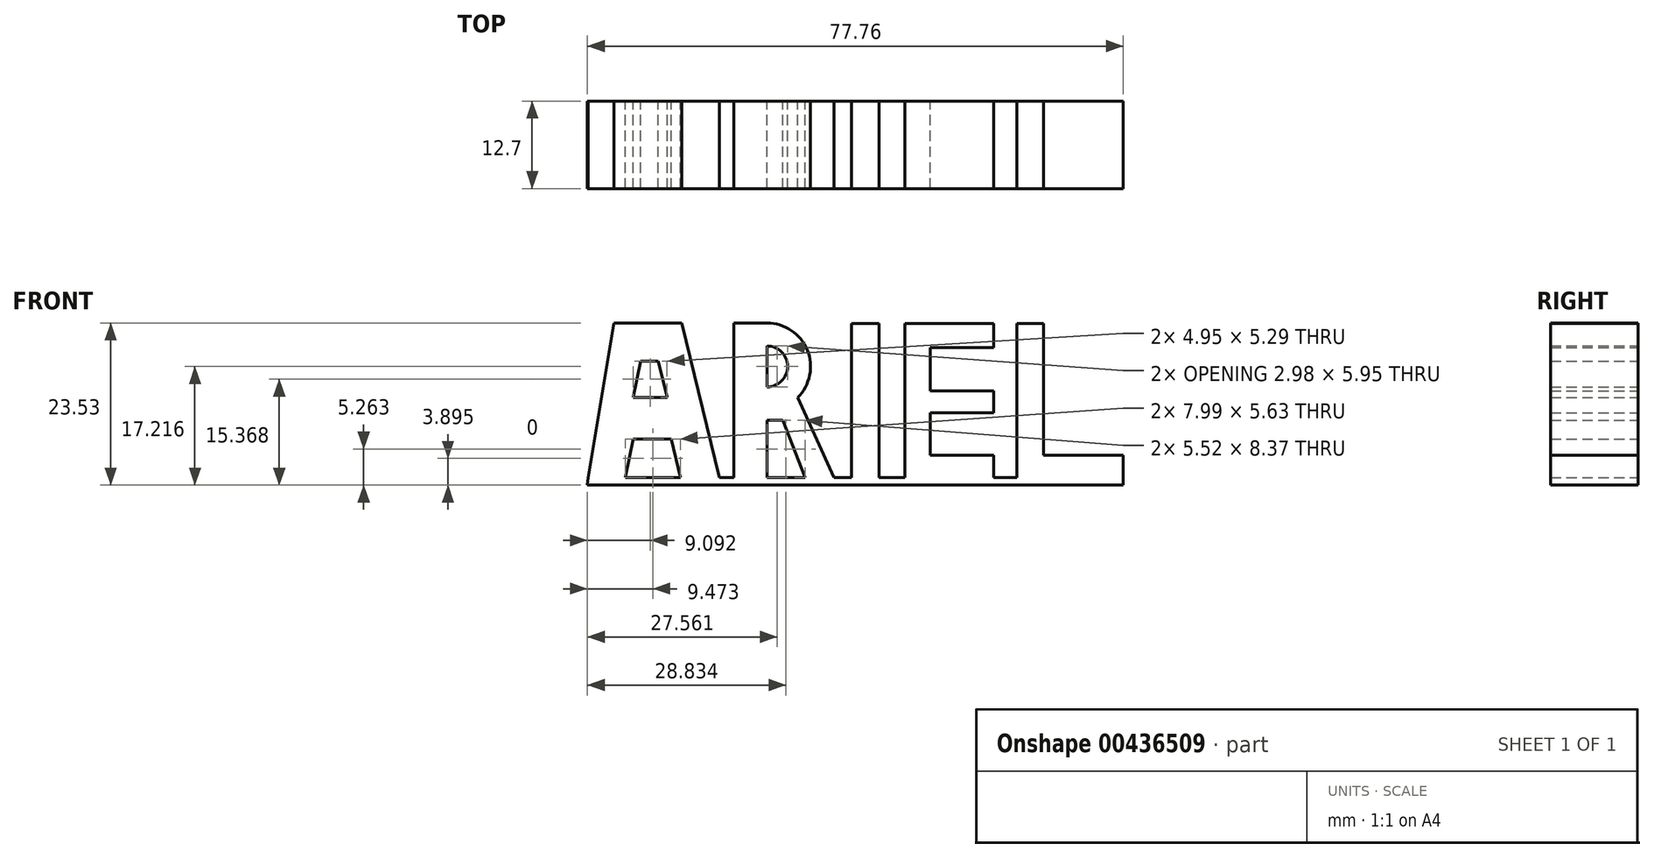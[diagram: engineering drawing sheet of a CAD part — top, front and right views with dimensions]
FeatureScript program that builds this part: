
annotation { "Feature Type Name" : "Feature", "Feature Type Description" : "" }
export const myFeature = defineFeature(function(context is Context, id is Id, definition is map)
    precondition{}
    {
        {
            var Q0;
            Q0=qCreatedBy(makeId("Front.planeOp"),FACE);
            var sketch = newSketch(context, id + "F0", { "sketchPlane" : qUnion([Q0])});
            skLineSegment(sketch, "E0", {"start": v(-36.7, 0) * mm, "end": v(-32.9, 22.45) * mm});
            skLineSegment(sketch, "E1", {"start": v(-32.9, 22.45) * mm, "end": v(-23.07, 22.45) * mm});
            skLineSegment(sketch, "E2", {"start": v(-23.07, 22.45) * mm, "end": v(-17.6, 0) * mm});
            skLineSegment(sketch, "E3", {"start": v(-23.3, 0) * mm, "end": v(-24.6, 5.63) * mm});
            skLineSegment(sketch, "E4", {"start": v(-24.6, 5.63) * mm, "end": v(-30.15, 5.63) * mm});
            skLineSegment(sketch, "E5", {"start": v(-30.15, 5.63) * mm, "end": v(-31.3, 0) * mm});
            skLineSegment(sketch, "E6", {"start": v(-30.15, 11.64) * mm, "end": v(-25.2, 11.64) * mm});
            skLineSegment(sketch, "E7", {"start": v(-25.2, 11.64) * mm, "end": v(-26.5, 16.93) * mm});
            skLineSegment(sketch, "E8", {"start": v(-26.5, 16.93) * mm, "end": v(-29.02, 16.93) * mm});
            skLineSegment(sketch, "E9", {"start": v(-29.02, 16.93) * mm, "end": v(-30.15, 11.64) * mm});
            skLineSegment(sketch, "E10", {"start": v(-17.6, 0) * mm, "end": v(-15.54, 0) * mm});
            skLineSegment(sketch, "E11", {"start": v(-15.54, 0) * mm, "end": v(-15.54, 22.45) * mm});
            skLineSegment(sketch, "E12", {"start": v(-15.54, 22.45) * mm, "end": v(-10.7, 22.45) * mm});
            skLineSegment(sketch, "E13", {"start": v(-10.7, 0) * mm, "end": v(-10.7, 8.37) * mm});
            skLineSegment(sketch, "E14", {"start": v(-10.7, 8.37) * mm, "end": v(-8.43, 8.37) * mm});
            skLineSegment(sketch, "E15", {"start": v(-8.43, 8.37) * mm, "end": v(-5.18, 0) * mm});
            skLineSegment(sketch, "E16", {"start": v(-1.01, 0) * mm, "end": v(-6.26, 11.64) * mm});
            skArc(sketch, "E17", {"start": v(-6.26, 11.64) * mm, "mid": v(-4.86, 18.53) * mm, "end": v(-10.7, 22.45) * mm});
            skArc(sketch, "E18", {"start": v(-10.7, 13.16) * mm, "mid": v(-7.72, 16.14) * mm, "end": v(-10.7, 19.11) * mm});
            skLineSegment(sketch, "E19", {"start": v(-10.7, 19.11) * mm, "end": v(-10.7, 13.16) * mm});
            skLineSegment(sketch, "E20", {"start": v(-1.01, 0) * mm, "end": v(1.57, 0) * mm});
            skLineSegment(sketch, "E21", {"start": v(1.57, 0) * mm, "end": v(1.57, 22.35) * mm});
            skLineSegment(sketch, "E22", {"start": v(1.57, 22.35) * mm, "end": v(5.55, 22.35) * mm});
            skLineSegment(sketch, "E23", {"start": v(5.55, 22.35) * mm, "end": v(5.55, 0) * mm});
            skLineSegment(sketch, "E24", {"start": v(5.55, 0) * mm, "end": v(9.3, 0) * mm});
            skLineSegment(sketch, "E25", {"start": v(9.3, 0) * mm, "end": v(9.3, 22.35) * mm});
            skLineSegment(sketch, "E26", {"start": v(9.3, 22.35) * mm, "end": v(22.2, 22.35) * mm});
            skLineSegment(sketch, "E27", {"start": v(22.2, 22.35) * mm, "end": v(22.2, 18.86) * mm});
            skLineSegment(sketch, "E28", {"start": v(22.2, 18.86) * mm, "end": v(13.02, 18.86) * mm});
            skLineSegment(sketch, "E29", {"start": v(13.02, 18.86) * mm, "end": v(13.02, 12.62) * mm});
            skLineSegment(sketch, "E30", {"start": v(13.02, 12.62) * mm, "end": v(22.2, 12.62) * mm});
            skLineSegment(sketch, "E31", {"start": v(22.2, 12.62) * mm, "end": v(22.2, 9.45) * mm});
            skLineSegment(sketch, "E32", {"start": v(22.2, 9.45) * mm, "end": v(13.02, 9.45) * mm});
            skLineSegment(sketch, "E33", {"start": v(13.02, 9.45) * mm, "end": v(13.02, 3.25) * mm});
            skLineSegment(sketch, "E34", {"start": v(13.02, 3.25) * mm, "end": v(22.2, 3.25) * mm});
            skLineSegment(sketch, "E35", {"start": v(22.2, 3.25) * mm, "end": v(22.2, 0) * mm});
            skLineSegment(sketch, "E36", {"start": v(22.2, 0) * mm, "end": v(25.55, 0) * mm});
            skLineSegment(sketch, "E37", {"start": v(25.55, 0) * mm, "end": v(25.55, 22.35) * mm});
            skLineSegment(sketch, "E38", {"start": v(25.55, 22.35) * mm, "end": v(29.42, 22.35) * mm});
            skLineSegment(sketch, "E39", {"start": v(29.42, 22.35) * mm, "end": v(29.42, 3.25) * mm});
            skLineSegment(sketch, "E40", {"start": v(29.42, 3.25) * mm, "end": v(41, 3.25) * mm});
            skLineSegment(sketch, "E41", {"start": v(41, 3.25) * mm, "end": v(41, 0) * mm});
            skLineSegment(sketch, "E42", {"start": v(41, 0) * mm, "end": v(41, -1.08) * mm});
            skLineSegment(sketch, "E43", {"start": v(41, -1.08) * mm, "end": v(-36.77, -1.08) * mm});
            skLineSegment(sketch, "E44", {"start": v(-36.77, -1.08) * mm, "end": v(-36.7, 0) * mm});
            skLineSegment(sketch, "E45", {"start": v(-31.3, 0) * mm, "end": v(-23.3, 0) * mm});
            skLineSegment(sketch, "E46", {"start": v(-10.7, 0) * mm, "end": v(-5.18, 0) * mm});
            skSolve(sketch);
        }
        {
            var Q0;
            Q0=makeQuery(id+"F0.imprint","IMPRINT",FACE,{"disambiguationData":[TD([[makeQuery(id+"F0.imprint","IMPRINT",EDGE,{"derivedFrom":sQuery(id+"F0.wireOp",EDGE,"E0")}),-1.0]])]});
            extrude(context, id + "F1", {"entities" : qUnion([Q0]), "depth" : 12.7 * mm});
        }
    });
